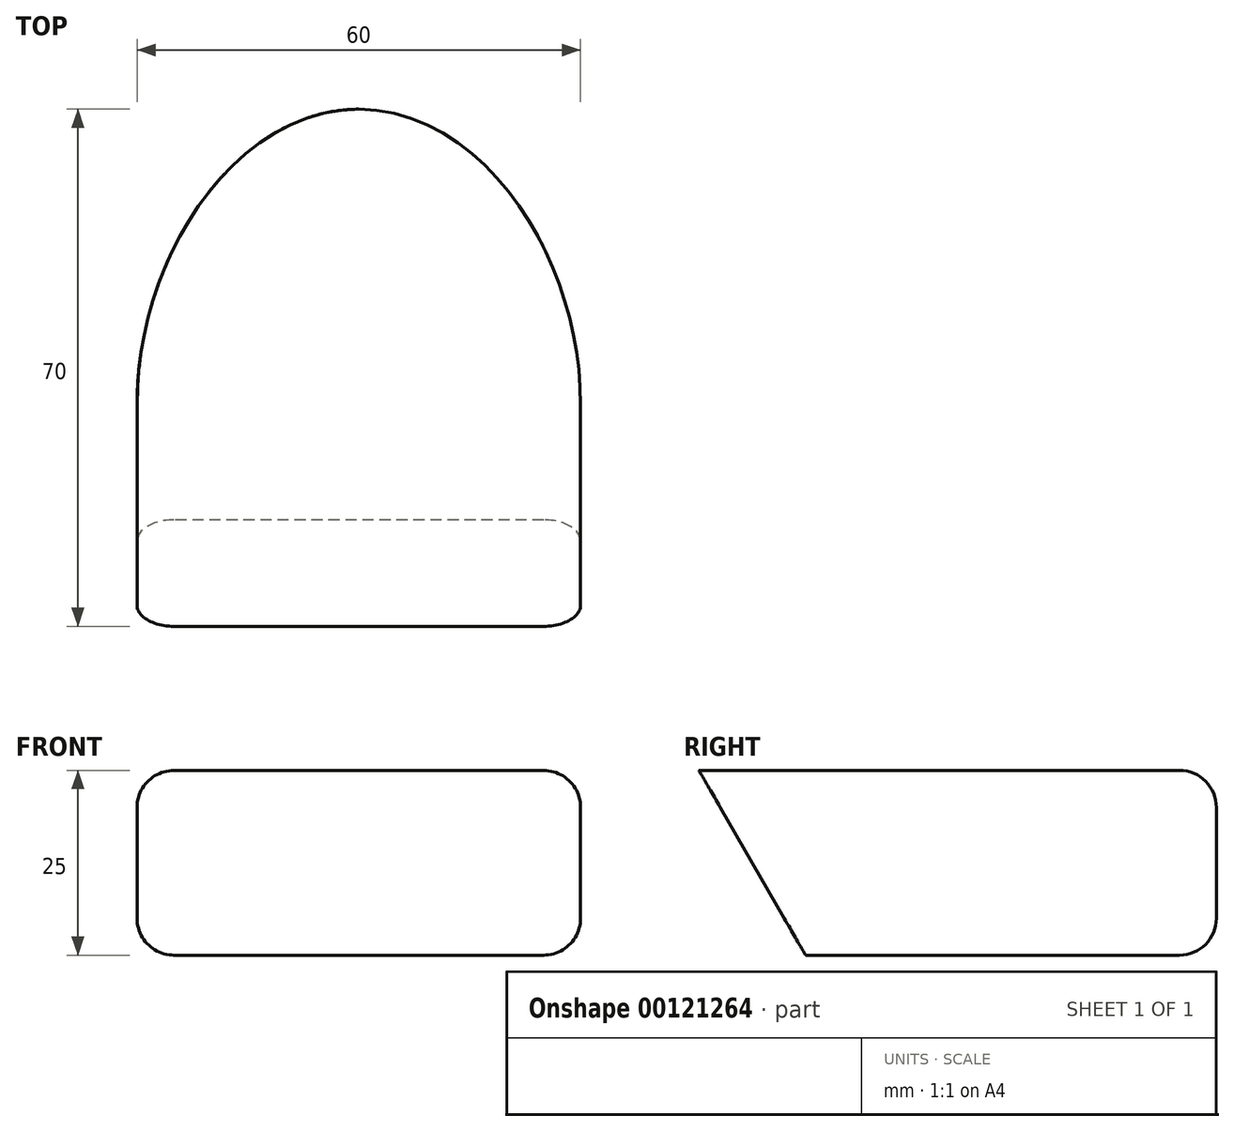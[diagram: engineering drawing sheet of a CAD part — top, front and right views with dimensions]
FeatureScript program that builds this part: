
annotation { "Feature Type Name" : "Feature", "Feature Type Description" : "" }
export const myFeature = defineFeature(function(context is Context, id is Id, definition is map)
    precondition{}
    {
        {
            var Q0;
            Q0=qCreatedBy(makeId("Top.planeOp"),FACE);
            var sketch = newSketch(context, id + "F0", { "sketchPlane" : qUnion([Q0])});
            skLineSegment(sketch, "E0.top", {"start": v(-30, -30) * mm, "end": v(30, -30) * mm});
            skPoint(sketch, "E0.middle", {"position": v(0, 0) * mm});
            skCircle(sketch, "E1", {"center": v(0, 0) * mm, "radius": 30 * mm});
            skPoint(sketch, "E2.visualSharp", {"position": v(-30, -30) * mm});
            skPoint(sketch, "E3.visualSharp", {"position": v(30, -30) * mm});
            skPoint(sketch, "E4", {"position": v(-30, 0) * mm});
            skPoint(sketch, "E5", {"position": v(30, 0) * mm});
            skFitSpline(sketch, "E6", {"points": [v(0, 40) * mm, v(-30, 0) * mm], "startDerivative": vector(-49.89, 0) * mm, "endDerivative": vector(0, -60.15) * mm});
            skFitSpline(sketch, "E7.MirrorCS", {"points": [v(0, 40) * mm, v(30, 0) * mm], "startDerivative": vector(49.89, 0) * mm, "endDerivative": vector(0, -60.15) * mm});
            skLineSegment(sketch, "E8", {"start": v(-30, 0) * mm, "end": v(-30, -30) * mm});
            skLineSegment(sketch, "E9", {"start": v(30, 0) * mm, "end": v(30, -30) * mm});
            skSolve(sketch);
        }
        {
            var Q0;
            Q0=qSketchRegion(id+"F0",true);
            extrude(context, id + "F1", {"entities" : qUnion([Q0]), "endBound" : BoundingType.SYMMETRIC, "depth" : 25 * mm});
        }
        {
            var Q0;
            Q0=makeQuery(id+"F1.opExtrude","CAP_EDGE",EDGE,{"disambiguationData":[OSD([sQuery(id+"F0.wireOp",EDGE,"E9")])],"isStart":true});
            var Q1;
            Q1=makeQuery(id+"F1.opExtrude","CAP_EDGE",EDGE,{"disambiguationData":[OSD([sQuery(id+"F0.wireOp",EDGE,"E9")])],"isStart":false});
            var Q2;
            Q2=makeQuery(id+"F1.opExtrude","CAP_EDGE",EDGE,{"disambiguationData":[OSD([sQuery(id+"F0.wireOp",EDGE,"E8")])],"isStart":false});
            var Q3;
            Q3=makeQuery(id+"F1.opExtrude","CAP_EDGE",EDGE,{"disambiguationData":[OSD([sQuery(id+"F0.wireOp",EDGE,"E8")])],"isStart":true});
            fillet(context, id + "F2", {"entities" : qUnion([Q0, Q1, Q2, Q3]), "radius" : 5 * mm, "tangentPropagation" : true, "allowEdgeOverflow" : false});
        }
        {
            var Q0;
            Q0=qCreatedBy(makeId("Right.planeOp"),FACE);
            var sketch = newSketch(context, id + "F3", { "sketchPlane" : qUnion([Q0])});
            skLineSegment(sketch, "E10", {"start": v(0, 0) * mm, "end": v(-30, 0) * mm});
            skPoint(sketch, "E11", {"position": v(-30, 0) * mm});
            skLineSegment(sketch, "E12", {"start": v(-30, 12.5) * mm, "end": v(-30, -12.5) * mm});
            skLineSegment(sketch, "E13", {"start": v(-30, -12.5) * mm, "end": v(0, -12.5) * mm});
            skLineSegment(sketch, "E14", {"start": v(-30, 12.5) * mm, "end": v(-15.57, -12.5) * mm});
            skLineSegment(sketch, "E15", {"start": v(-30, 7.5) * mm, "end": v(-27.11, 7.5) * mm});
            skSolve(sketch);
        }
        {
            var Q0;
            {var subQ0=sQuery(id+"F3.wireOp",EDGE,"E12");var subQ1=sQuery(id+"F3.wireOp",EDGE,"E10");var subQ2=makeQuery(id+"F3.imprint","INTERSECT",VERTEX,{"derivedFrom":[subQ1,subQ0]});Q0=makeQuery(id+"F3.imprint","IMPRINT",FACE,{"disambiguationData":[TD([[makeQuery(id+"F3.imprint","IMPRINT",EDGE,{"disambiguationData":[TD([[subQ2,1.0]])],"derivedFrom":subQ1}),1.0]])]});}
            var Q1;
            {var subQ0=sQuery(id+"F3.wireOp",EDGE,"E12");var subQ1=sQuery(id+"F3.wireOp",EDGE,"E10");var subQ2=makeQuery(id+"F3.imprint","INTERSECT",VERTEX,{"derivedFrom":[subQ1,subQ0]});Q1=makeQuery(id+"F3.imprint","IMPRINT",FACE,{"disambiguationData":[TD([[makeQuery(id+"F3.imprint","IMPRINT",EDGE,{"disambiguationData":[TD([[subQ2,1.0]])],"derivedFrom":subQ1}),-1.0]])]});}
            var Q2;
            {var subQ3=sQuery(id+"F3.wireOp",EDGE,"E15");Q2=makeQuery(id+"F3.imprint","IMPRINT",FACE,{"disambiguationData":[TD([[makeQuery(id+"F3.imprint","IMPRINT",EDGE,{"derivedFrom":subQ3}),1.0]])]});}
            extrude(context, id + "F4", {"entities" : qUnion([Q0, Q1, Q2]), "operationType" : NewBodyOperationType.REMOVE, "endBound" : BoundingType.SYMMETRIC, "depth" : 60 * mm});
        }
    });
